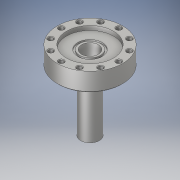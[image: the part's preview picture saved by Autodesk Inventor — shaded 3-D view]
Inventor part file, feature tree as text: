
AUTODESK INVENTOR PART (.ipt)
format: ipt  version: 2018 (Build 220112000, 112)  size: 207,360 bytes
history: native  units: in
note: dims shown in document units (in); Inventor stores cm internally (conversion verified against a paired STEP export)
features: sketch x6, extrude x5, chamfer x3, hole x1, pattern_circular x1
ambient origin geometry x8: Origin, YZ Plane, XZ Plane, XY Plane, X Axis, Y Axis, Z Axis, Center Point
bodies: Solid1 (feature_tree)
feature tree (16):
  extrude  "Extrusion1"  Depth=0.5in TaperAngle=0.0deg
  chamfer  "Chamfer1"  Distance=0.0291in Angle=45.0deg
  extrude  "Extrusion2"  Depth=0.113in TaperAngle=0.0deg
  extrude  "Extrusion3"  Depth=0.05in
  extrude  "Extrusion4"  Depth=0.5in
  chamfer  "Chamfer2"  Distance=0.04in
  extrude  "Extrusion5"  Depth=0.45in
  hole  "Hole1"  [1 undecoded]
  chamfer  "Chamfer3"  Angle=30.0deg  [1 undecoded]
  pattern_circular  "Circular Pattern1"  Angle=45.0deg  [1 undecoded]
  sketch  "Sketch1"  dims[d0=1.755in d1=0.5in d2=0.0in d3=0.0291in d4=0.125in d5=45.0deg]
  sketch  "Sketch2"  dims[d6=1.26in d7=0.113in d8=0.0in]
  sketch  "Sketch3"  dims[d9=0.658in d10=0.05in]
  sketch  "Sketch4"  dims[d11=0.04in d12=0.0in d13=0.5in d14=0.04in d15=0.0in]
  sketch  "Sketch5"  dims[d16=0.0291in d17=0.125in d18=45.0deg d19=0.45in]
  sketch  "Sketch6"  dims[d20=2.0in d21=0.0in d22=0.775in d23=30.0deg d24=0.125in d25=0.75in d26=0.375in d27=0.25in d28=0.5635in d29=1.0in d30=0.8108in d31=0.015in d32=0.125in d33=45.0deg d34=4.7244in d35=360.0deg]
note: 3 required parameter values undecoded (feature->parameter linkage not recoverable at this tier; creation-order binding heuristic only, values carry confidence <= 0.55)
